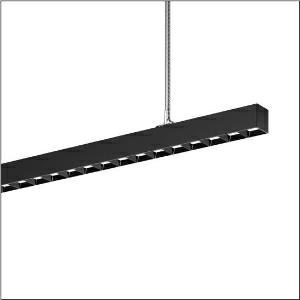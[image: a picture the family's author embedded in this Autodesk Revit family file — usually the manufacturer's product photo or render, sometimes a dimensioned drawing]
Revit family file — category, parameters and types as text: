
# Revit family: silica_r__21_51mx32tctdb_2a66
name_source: partatom
category: Lighting Fixtures
units: mm (PartAtom-declared; Revit-internal decimal feet)

## family parameters
Cut with Voids When Loaded = No
Host = Face
Light Source = No
Part Type = Normal
Room Calculation Point = No
Round Connector Dimension = Use Diameter
Shared = No

## types (1)
- --- (1 x LED, 15540 lm, 133.6 W, 6500K)
    Apparent Load = 134 VA
    CIE Flux Codes = 84 99 100 60 100
    Color Rendering = 80
    Color Temperature = 6500K
    Default Elevation = 1800 mm
    Description = Silica® 21, office luminaire, primary light control with darklight reflector, of PMMA, black, CAT 2 (L<= 3000cd/m²), light emission: direct/indirect distribution, primary light characteristic: symmetric, installation type: suspended mounting, LED, rated luminous flux: 15.540lm, luminous efficacy: 111lm/W, light colour: 8tw, colour temperature: 2700..6500K, control gear: ECG DALI, with terminal, 3+2-pole, max. 2.5mm², mains connection: 220..240V, AC, 50/60Hz, rated input power: 140.3W, luminaire housing, of aluminium, jet black (RAL 9005), length: 3.004mm, width: 53mm, height: 53mm, protection rating (complete): IP20, insulation class (complete): insulation class I (protective earthing), certification: CE, permissible operating ambient temperature: 0..+35°C, standard: EN 50419, packaging unit: 1 piece
    Height = 53 mm
    Lamp = 1 x LED
    Lamp Light Flux = 15540 lm
    Lamp Power = 133.6 W
    Lamp count = 1
    Length = 3004 mm
    Luminous efficacy = 116 lm/W
    Manufacturer = Siteco
    ModVariant = No
    Model = 51MX32TCTDB
    Mounting Place = Ceiling
    Mounting Type = Pendant
    Number of Poles = 1
    OnlyDefault = Yes
    Power Factor = 1
    Product Name = Silica® 21
    Product group = office luminaire | ceiling pendant
    ProductGroupID = 902
    Protection Class = Protection class I
    Protection Degree = IP 20
    RLX_Detail_Level = 1
    RLX_Emergency_Light_Flux = 0 lm
    RLX_Emergency_Type = 0
    RLX_Emergency_Type_DB = No
    RlxData = <blob elided: 63365 chars, md5=3504a17a>
    Socket = socket
    Standby Power = 0 W
    System Light Flux = 15540 lm
    System Power = 134 W
    Type Comments = individual setting
    Type Image = l_1313617.jpg
    URL = http://relux.com
    VarID = @adj_089301
    Voltage = 0 V
    Weight = 0.00 kg
    Width = 53 mm

## geometry (parser evidence)
native form markers: Blend x4, Sweep x11
no freeform markers — native parametric forms only
